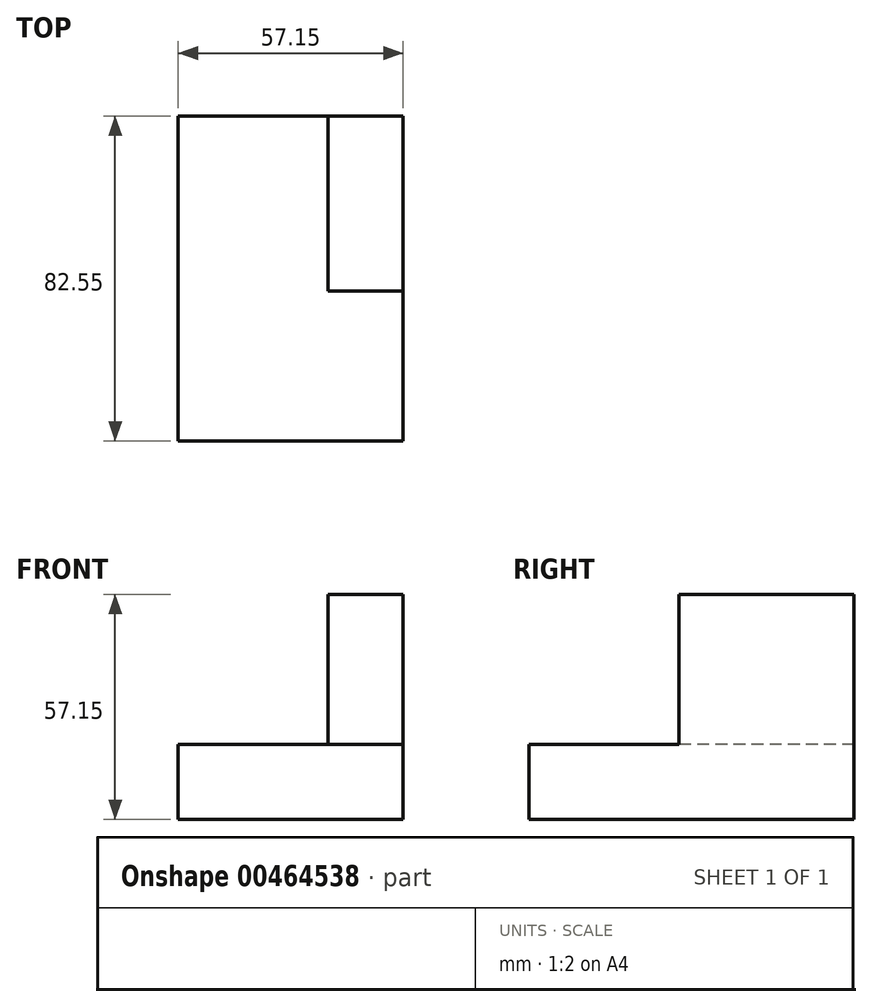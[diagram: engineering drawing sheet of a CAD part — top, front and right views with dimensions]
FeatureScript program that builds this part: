
annotation { "Feature Type Name" : "Feature", "Feature Type Description" : "" }
export const myFeature = defineFeature(function(context is Context, id is Id, definition is map)
    precondition{}
    {
        {
            var Q0;
            Q0=qCreatedBy(makeId("Right.planeOp"),FACE);
            var sketch = newSketch(context, id + "F0", { "sketchPlane" : qUnion([Q0])});
            skLineSegment(sketch, "E0.bottom", {"start": v(0, 0) * mm, "end": v(-19.05, 0) * mm});
            skLineSegment(sketch, "E0.top", {"start": v(0, 19.05) * mm, "end": v(-19.05, 19.05) * mm});
            skLineSegment(sketch, "E0.left", {"start": v(0, 0) * mm, "end": v(0, 19.05) * mm});
            skLineSegment(sketch, "E0.right", {"start": v(-19.05, 0) * mm, "end": v(-19.05, 19.05) * mm});
            skLineSegment(sketch, "E1.top", {"start": v(0, 57.15) * mm, "end": v(-19.05, 57.15) * mm});
            skLineSegment(sketch, "E1.left", {"start": v(0, 19.05) * mm, "end": v(0, 57.15) * mm});
            skLineSegment(sketch, "E1.right", {"start": v(-19.05, 19.05) * mm, "end": v(-19.05, 57.15) * mm});
            skLineSegment(sketch, "E2.bottom", {"start": v(-19.05, 19.05) * mm, "end": v(-57.15, 19.05) * mm});
            skLineSegment(sketch, "E2.top", {"start": v(-19.05, 0) * mm, "end": v(-57.15, 0) * mm});
            skLineSegment(sketch, "E2.left", {"start": v(-19.05, 19.05) * mm, "end": v(-19.05, 0) * mm});
            skLineSegment(sketch, "E2.right", {"start": v(-57.15, 19.05) * mm, "end": v(-57.15, 0) * mm});
            skSolve(sketch);
        }
        {
            var Q0;
            Q0=makeQuery(id+"F0.imprint","IMPRINT",FACE,{"disambiguationData":[TD([[makeQuery(id+"F0.imprint","IMPRINT",EDGE,{"derivedFrom":sQuery(id+"F0.wireOp",EDGE,"E0.top")}),-1.0]])]});
            var Q1;
            Q1=makeQuery(id+"F0.imprint","IMPRINT",FACE,{"disambiguationData":[TD([[makeQuery(id+"F0.imprint","IMPRINT",EDGE,{"derivedFrom":sQuery(id+"F0.wireOp",EDGE,"E0.bottom")}),-1.0]])]});
            var Q2;
            Q2=makeQuery(id+"F0.imprint","IMPRINT",FACE,{"disambiguationData":[TD([[makeQuery(id+"F0.imprint","IMPRINT",EDGE,{"derivedFrom":sQuery(id+"F0.wireOp",EDGE,"E2.bottom")}),1.0]])]});
            extrude(context, id + "F1", {"entities" : qUnion([Q0, Q1, Q2]), "depth" : 19.05 * mm});
        }
        {
            var Q0;
            Q0=makeQuery(id+"F1.opExtrude","CAP_FACE",FACE,{"disambiguationData":[OSD([sQuery(id+"F0.wireOp",EDGE,"E0.bottom"),sQuery(id+"F0.wireOp",EDGE,"E0.left"),sQuery(id+"F0.wireOp",EDGE,"E1.top"),sQuery(id+"F0.wireOp",EDGE,"E1.left"),sQuery(id+"F0.wireOp",EDGE,"E1.right"),sQuery(id+"F0.wireOp",EDGE,"E2.bottom"),sQuery(id+"F0.wireOp",EDGE,"E2.top"),sQuery(id+"F0.wireOp",EDGE,"E2.right")])],"isStart":true});
            var sketch = newSketch(context, id + "F2", { "sketchPlane" : qUnion([Q0])});
            skLineSegment(sketch, "E3.bottom", {"start": v(57.15, 0) * mm, "end": v(19.05, 0) * mm});
            skLineSegment(sketch, "E3.top", {"start": v(57.15, 19.05) * mm, "end": v(19.05, 19.05) * mm});
            skLineSegment(sketch, "E3.left", {"start": v(57.15, 0) * mm, "end": v(57.15, 19.05) * mm});
            skLineSegment(sketch, "E3.right", {"start": v(19.05, 0) * mm, "end": v(19.05, 19.05) * mm});
            skLineSegment(sketch, "E4.bottom", {"start": v(19.05, 19.05) * mm, "end": v(0, 19.05) * mm});
            skLineSegment(sketch, "E4.top", {"start": v(19.05, 0) * mm, "end": v(0, 0) * mm});
            skLineSegment(sketch, "E4.left", {"start": v(19.05, 19.05) * mm, "end": v(19.05, 0) * mm});
            skLineSegment(sketch, "E4.right", {"start": v(0, 19.05) * mm, "end": v(0, 0) * mm});
            skSolve(sketch);
        }
        {
            var Q0;
            Q0=makeQuery(id+"F2.imprint","IMPRINT",FACE,{"disambiguationData":[TD([[makeQuery(id+"F2.imprint","IMPRINT",EDGE,{"derivedFrom":sQuery(id+"F2.wireOp",EDGE,"E3.bottom")}),1.0]])]});
            var Q1;
            Q1=makeQuery(id+"F2.imprint","IMPRINT",FACE,{"disambiguationData":[TD([[makeQuery(id+"F2.imprint","IMPRINT",EDGE,{"derivedFrom":sQuery(id+"F2.wireOp",EDGE,"E4.bottom")}),1.0]])]});
            extrude(context, id + "F3", {"entities" : qUnion([Q0, Q1]), "operationType" : NewBodyOperationType.ADD, "depth" : 19.05 * mm});
        }
        {
            var Q0;
            Q0=makeQuery(id+"F3.opExtrude","CAP_FACE",FACE,{"disambiguationData":[OSD([sQuery(id+"F2.wireOp",EDGE,"E3.bottom"),sQuery(id+"F2.wireOp",EDGE,"E3.top"),sQuery(id+"F2.wireOp",EDGE,"E3.left"),sQuery(id+"F2.wireOp",EDGE,"E4.bottom"),sQuery(id+"F2.wireOp",EDGE,"E4.top"),sQuery(id+"F2.wireOp",EDGE,"E4.right")])],"isStart":false});
            var sketch = newSketch(context, id + "F4", { "sketchPlane" : qUnion([Q0])});
            skLineSegment(sketch, "E5.bottom", {"start": v(0, 19.05) * mm, "end": v(57.15, 19.05) * mm});
            skLineSegment(sketch, "E5.top", {"start": v(0, 0) * mm, "end": v(57.15, 0) * mm});
            skLineSegment(sketch, "E5.left", {"start": v(0, 19.05) * mm, "end": v(0, 0) * mm});
            skLineSegment(sketch, "E5.right", {"start": v(57.15, 19.05) * mm, "end": v(57.15, 0) * mm});
            skLineSegment(sketch, "E6.bottom", {"start": v(0, 19.05) * mm, "end": v(19.05, 19.05) * mm});
            skLineSegment(sketch, "E6.top", {"start": v(0, 57.15) * mm, "end": v(19.05, 57.15) * mm});
            skLineSegment(sketch, "E6.left", {"start": v(0, 19.05) * mm, "end": v(0, 57.15) * mm});
            skLineSegment(sketch, "E6.right", {"start": v(19.05, 19.05) * mm, "end": v(19.05, 57.15) * mm});
            skSolve(sketch);
        }
        {
            var Q0;
            Q0=makeQuery(id+"F4.imprint","IMPRINT",FACE,{"disambiguationData":[TD([[makeQuery(id+"F4.imprint","IMPRINT",EDGE,{"derivedFrom":sQuery(id+"F4.wireOp",EDGE,"E6.bottom")}),1.0]])]});
            var Q1;
            Q1=makeQuery(id+"F4.imprint","IMPRINT",FACE,{"disambiguationData":[TD([[makeQuery(id+"F4.imprint","IMPRINT",EDGE,{"derivedFrom":sQuery(id+"F4.wireOp",EDGE,"E5.bottom")}),-1.0]])]});
            extrude(context, id + "F5", {"entities" : qUnion([Q0, Q1]), "operationType" : NewBodyOperationType.ADD, "depth" : 19.05 * mm});
        }
        {
            var Q0;
            Q0=makeQuery(id+"F5.boolean.opBoolean","MERGE",FACE,{"derivedFrom":[makeQuery(id+"F3.boolean.opBoolean","MERGE",FACE,{"derivedFrom":[makeQuery(id+"F1.opExtrude","SWEPT_FACE",FACE,{"disambiguationData":[OSD([sQuery(id+"F0.wireOp",EDGE,"E0.left"),sQuery(id+"F0.wireOp",EDGE,"E1.left")])]}),makeQuery(id+"F3.opExtrude","SWEPT_FACE",FACE,{"disambiguationData":[OSD([sQuery(id+"F2.wireOp",EDGE,"E4.right")])]})]}),makeQuery(id+"F5.opExtrude","SWEPT_FACE",FACE,{"disambiguationData":[OSD([sQuery(id+"F4.wireOp",EDGE,"E5.left"),sQuery(id+"F4.wireOp",EDGE,"E6.left")])]})]});
            extrude(context, id + "F6", {"entities" : qUnion([Q0]), "operationType" : NewBodyOperationType.ADD, "depth" : 25.4 * mm});
        }
    });
